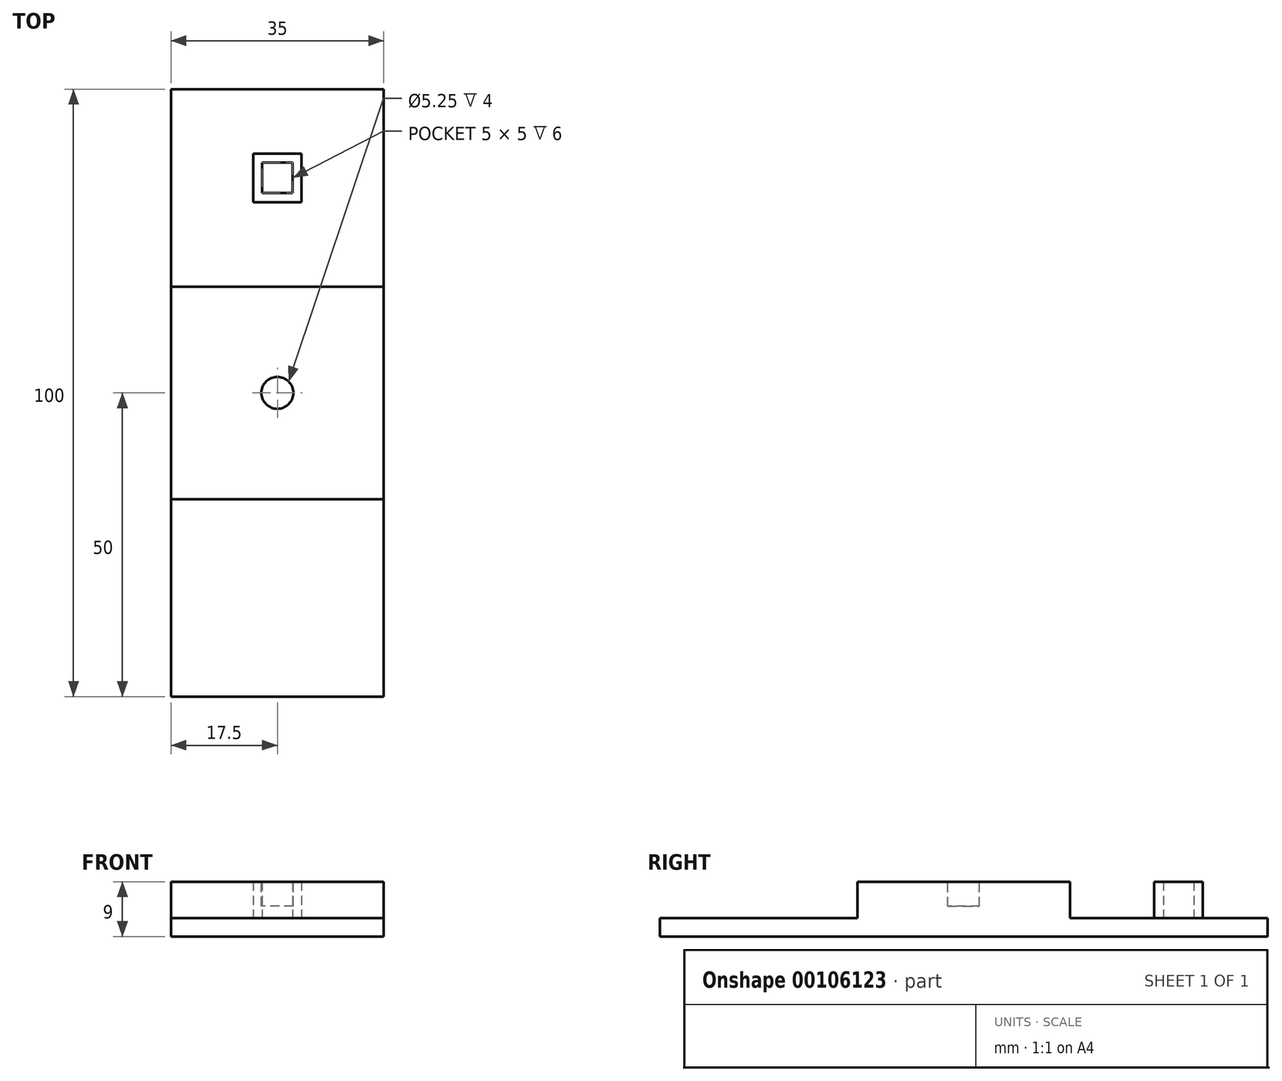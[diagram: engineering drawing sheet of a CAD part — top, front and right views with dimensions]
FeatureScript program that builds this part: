
annotation { "Feature Type Name" : "Feature", "Feature Type Description" : "" }
export const myFeature = defineFeature(function(context is Context, id is Id, definition is map)
    precondition{}
    {
        {
            var Q0;
            Q0=qCreatedBy(makeId("Top.planeOp"),FACE);
            var sketch = newSketch(context, id + "F0", { "sketchPlane" : qUnion([Q0])});
            skLineSegment(sketch, "E0.bottom", {"start": v(-17.5, 50) * mm, "end": v(17.5, 50) * mm});
            skLineSegment(sketch, "E0.top", {"start": v(-17.5, -50) * mm, "end": v(17.5, -50) * mm});
            skLineSegment(sketch, "E0.left", {"start": v(-17.5, 50) * mm, "end": v(-17.5, -50) * mm});
            skLineSegment(sketch, "E0.right", {"start": v(17.5, 50) * mm, "end": v(17.5, -50) * mm});
            skPoint(sketch, "E0.middle", {"position": v(0, 0) * mm});
            skSolve(sketch);
        }
        {
            var Q0;
            Q0=makeQuery(id+"F0.imprint","IMPRINT",FACE,{"disambiguationData":[TD([[makeQuery(id+"F0.imprint","IMPRINT",EDGE,{"derivedFrom":sQuery(id+"F0.wireOp",EDGE,"E0.bottom")}),-1.0]])]});
            extrude(context, id + "F1", {"entities" : qUnion([Q0]), "depth" : 3 * mm});
        }
        {
            var Q0;
            Q0=makeQuery(id+"F1.opExtrude","CAP_FACE",FACE,{"disambiguationData":[OSD([sQuery(id+"F0.wireOp",EDGE,"E0.bottom"),sQuery(id+"F0.wireOp",EDGE,"E0.top"),sQuery(id+"F0.wireOp",EDGE,"E0.left"),sQuery(id+"F0.wireOp",EDGE,"E0.right")])],"isStart":false});
            var sketch = newSketch(context, id + "F2", { "sketchPlane" : qUnion([Q0])});
            skLineSegment(sketch, "E1.bottom", {"start": v(-17.5, 17.5) * mm, "end": v(17.5, 17.5) * mm});
            skLineSegment(sketch, "E1.top", {"start": v(-17.5, -17.5) * mm, "end": v(17.5, -17.5) * mm});
            skLineSegment(sketch, "E1.left", {"start": v(-17.5, 17.5) * mm, "end": v(-17.5, -17.5) * mm});
            skLineSegment(sketch, "E1.right", {"start": v(17.5, 17.5) * mm, "end": v(17.5, -17.5) * mm});
            skPoint(sketch, "E1.middle", {"position": v(0, 0) * mm});
            skSolve(sketch);
        }
        {
            var Q0;
            Q0=makeQuery(id+"F2.imprint","IMPRINT",FACE,{"disambiguationData":[TD([[makeQuery(id+"F2.imprint","IMPRINT",EDGE,{"derivedFrom":sQuery(id+"F2.wireOp",EDGE,"E1.bottom")}),-1.0]])]});
            extrude(context, id + "F3", {"entities" : qUnion([Q0]), "operationType" : NewBodyOperationType.ADD, "depth" : 6 * mm});
        }
        {
            var Q0;
            Q0=makeQuery(id+"F3.opExtrude","CAP_FACE",FACE,{"disambiguationData":[OSD([sQuery(id+"F2.wireOp",EDGE,"E1.bottom"),sQuery(id+"F2.wireOp",EDGE,"E1.top"),sQuery(id+"F2.wireOp",EDGE,"E1.left"),sQuery(id+"F2.wireOp",EDGE,"E1.right")])],"isStart":false});
            var sketch = newSketch(context, id + "F4", { "sketchPlane" : qUnion([Q0])});
            skCircle(sketch, "E2", {"center": v(0, 0) * mm, "radius": 2.62 * mm});
            skSolve(sketch);
        }
        {
            var Q0;
            Q0=makeQuery(id+"F4.imprint","IMPRINT",FACE,{"disambiguationData":[TD([[makeQuery(id+"F4.imprint","IMPRINT",EDGE,{"derivedFrom":sQuery(id+"F4.wireOp",EDGE,"E2")}),1.0]])]});
            extrude(context, id + "F5", {"entities" : qUnion([Q0]), "operationType" : NewBodyOperationType.REMOVE, "oppositeDirection" : true, "depth" : 4 * mm});
        }
        {
            var Q0;
            {var subQ0=sQuery(id+"F0.wireOp",EDGE,"E0.right");var subQ1=sQuery(id+"F0.wireOp",EDGE,"E0.left");var subQ2=sQuery(id+"F0.wireOp",EDGE,"E0.bottom");Q0=makeQuery(id+"F3.boolean.opBoolean","SPLIT",FACE,{"disambiguationData":[TD([makeQuery(id+"F1.opExtrude","SWEPT_FACE",FACE,{"disambiguationData":[OSD([subQ2])]})])],"derivedFrom":makeQuery(id+"F1.opExtrude","CAP_FACE",FACE,{"disambiguationData":[OSD([subQ2,sQuery(id+"F0.wireOp",EDGE,"E0.top"),subQ1,subQ0])],"isStart":false})});}
            var sketch = newSketch(context, id + "F6", { "sketchPlane" : qUnion([Q0])});
            skLineSegment(sketch, "E3.bottom", {"start": v(-2.5, 37.9) * mm, "end": v(2.5, 37.9) * mm});
            skLineSegment(sketch, "E3.top", {"start": v(-2.5, 32.9) * mm, "end": v(2.5, 32.9) * mm});
            skLineSegment(sketch, "E3.left", {"start": v(-2.5, 37.9) * mm, "end": v(-2.5, 32.9) * mm});
            skLineSegment(sketch, "E3.right", {"start": v(2.5, 37.9) * mm, "end": v(2.5, 32.9) * mm});
            skPoint(sketch, "E3.middle", {"position": v(0, 35.4) * mm});
            skLineSegment(sketch, "E4.bottom", {"start": v(-4, 39.4) * mm, "end": v(4, 39.4) * mm});
            skLineSegment(sketch, "E4.top", {"start": v(-4, 31.4) * mm, "end": v(4, 31.4) * mm});
            skLineSegment(sketch, "E4.left", {"start": v(-4, 39.4) * mm, "end": v(-4, 31.4) * mm});
            skLineSegment(sketch, "E4.right", {"start": v(4, 39.4) * mm, "end": v(4, 31.4) * mm});
            skSolve(sketch);
        }
        {
            var Q0;
            Q0=makeQuery(id+"F6.imprint","IMPRINT",FACE,{"disambiguationData":[TD([[makeQuery(id+"F6.imprint","IMPRINT",EDGE,{"derivedFrom":sQuery(id+"F6.wireOp",EDGE,"E3.bottom")}),1.0]])]});
            extrude(context, id + "F7", {"entities" : qUnion([Q0]), "operationType" : NewBodyOperationType.ADD, "depth" : 6 * mm});
        }
    });
